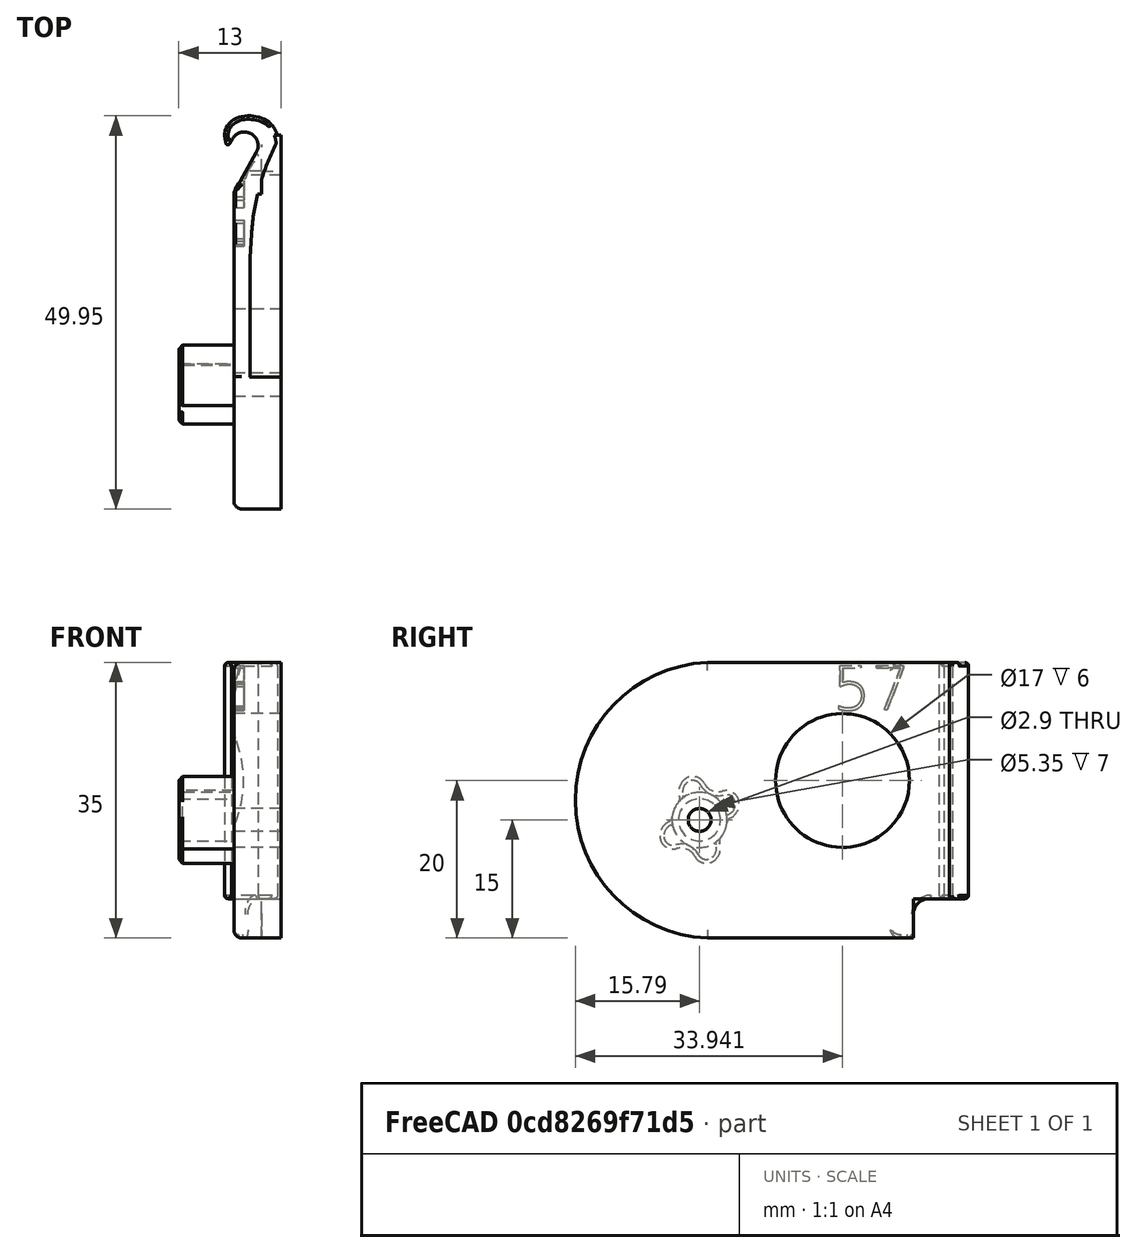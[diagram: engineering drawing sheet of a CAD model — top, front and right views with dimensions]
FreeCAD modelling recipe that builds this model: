
FCSTD DOCUMENT  (FreeCAD 0.18R)
Label: hinge-right-157deg-flat
License: All rights reserved
LicenseURL: http://en.wikipedia.org/wiki/All_rights_reserved
objects: App::FeaturePython×4, Part::FeaturePython×2, Part::Part2DObjectPython×1, Part::Extrusion×1, Part::Cut×1
note: 5 computed .brp shape members not serialized (recipe doc carries the construction recipe); baked Part::Feature solids carry a one-line shape summary decoded from their .brp

FEATURE [Part::FeaturePython] pillar_base_001  label="pillar-base_001"  # a2plus imported part (geometry in sourceFile) (typed FeaturePython)
  Placement = pos=(0.000608724,-56.8162,25.2903) rot=(-1,0,0;0.837584rad)
  a2p_Version = V0.1
  fixedPosition = false
  objectType = a2pPart
  sourceFile = ./parts/pillar-base.fcstd
  subassemblyImport = false
  timeLastImport = 1.60452e+09
  updateColors = true
FEATURE [Part::Part2DObjectPython] ShapeString  # Draft 2D object (typed FeaturePython)
  FontFile = <path>
  Placement = pos=(1.61,10.5,29) rot=(0.57735,-0.57735,-0.57735;2.0944rad)
  Size = 6
  String = 57
  Tracking = 0
FEATURE [Part::Extrusion] Extrude
  Base = -> ShapeString
  Dir = (-1,0,0)
  DirMode = 2
  FaceMakerClass = Part::FaceMakerBullseye
  LengthFwd = 3.5
  LengthRev = 0
  Placement = pos=(0,0,0) rot=(0,0,1;3.14159rad)
  Solid = false
  Symmetric = false
FEATURE [Part::FeaturePython] bracket_right_flat_001  label="bracket-right-flat_001"  # a2plus imported part (geometry in sourceFile) (typed FeaturePython)
  Placement = pos=(0,0,0) rot=(0,0,1;3.14159rad)
  a2p_Version = V0.1
  fixedPosition = true
  objectType = a2pPart
  sourceFile = ./parts/bracket-right-flat.fcstd
  subassemblyImport = false
  timeLastImport = 1.60489e+09
  updateColors = true
FEATURE [App::FeaturePython] axisCoincident_001  label="axisCoincident_001__bracket-right-flat_001"  # a2plus constraint (typed FeaturePython)
  Object1 = pillar_base_001
  Object2 = bracket_right_flat_001
  ParentTreeObject = -> pillar_base_001
  SubElement1 = Face17
  SubElement2 = Face31
  Suppressed = false
  Type = axial
  directionConstraint = 1
  lockRotation = false
FEATURE [App::FeaturePython] axisCoincident_001_mirror  label="axisCoincident_001__pillar-base_001"  # a2plus constraint (typed FeaturePython)
  Object1 = pillar_base_001
  Object2 = bracket_right_flat_001
  ParentTreeObject = -> bracket_right_flat_001
  SubElement1 = Face17
  SubElement2 = Face31
  Suppressed = false
  Type = axial
  directionConstraint = 1
  lockRotation = false
FEATURE [App::FeaturePython] planeCoincident_001  label="planeCoincident_001__bracket-right-flat_001"  # a2plus constraint (typed FeaturePython)
  Object1 = pillar_base_001
  Object2 = bracket_right_flat_001
  ParentTreeObject = -> pillar_base_001
  SubElement1 = Face1
  SubElement2 = Face57
  Suppressed = false
  Type = plane
  directionConstraint = 1
  offset = 0
FEATURE [App::FeaturePython] planeCoincident_001_mirror  label="planeCoincident_001__pillar-base_001"  # a2plus constraint (typed FeaturePython)
  Object1 = pillar_base_001
  Object2 = bracket_right_flat_001
  ParentTreeObject = -> bracket_right_flat_001
  SubElement1 = Face1
  SubElement2 = Face57
  Suppressed = false
  Type = plane
  directionConstraint = 1
  offset = 0
FEATURE [Part::Cut] Cut
  Base = -> bracket_right_flat_001
  Tool = -> Extrude
note: 1 file-system path scrubbed to <path> (originals preserved in the JSON sidecar)
